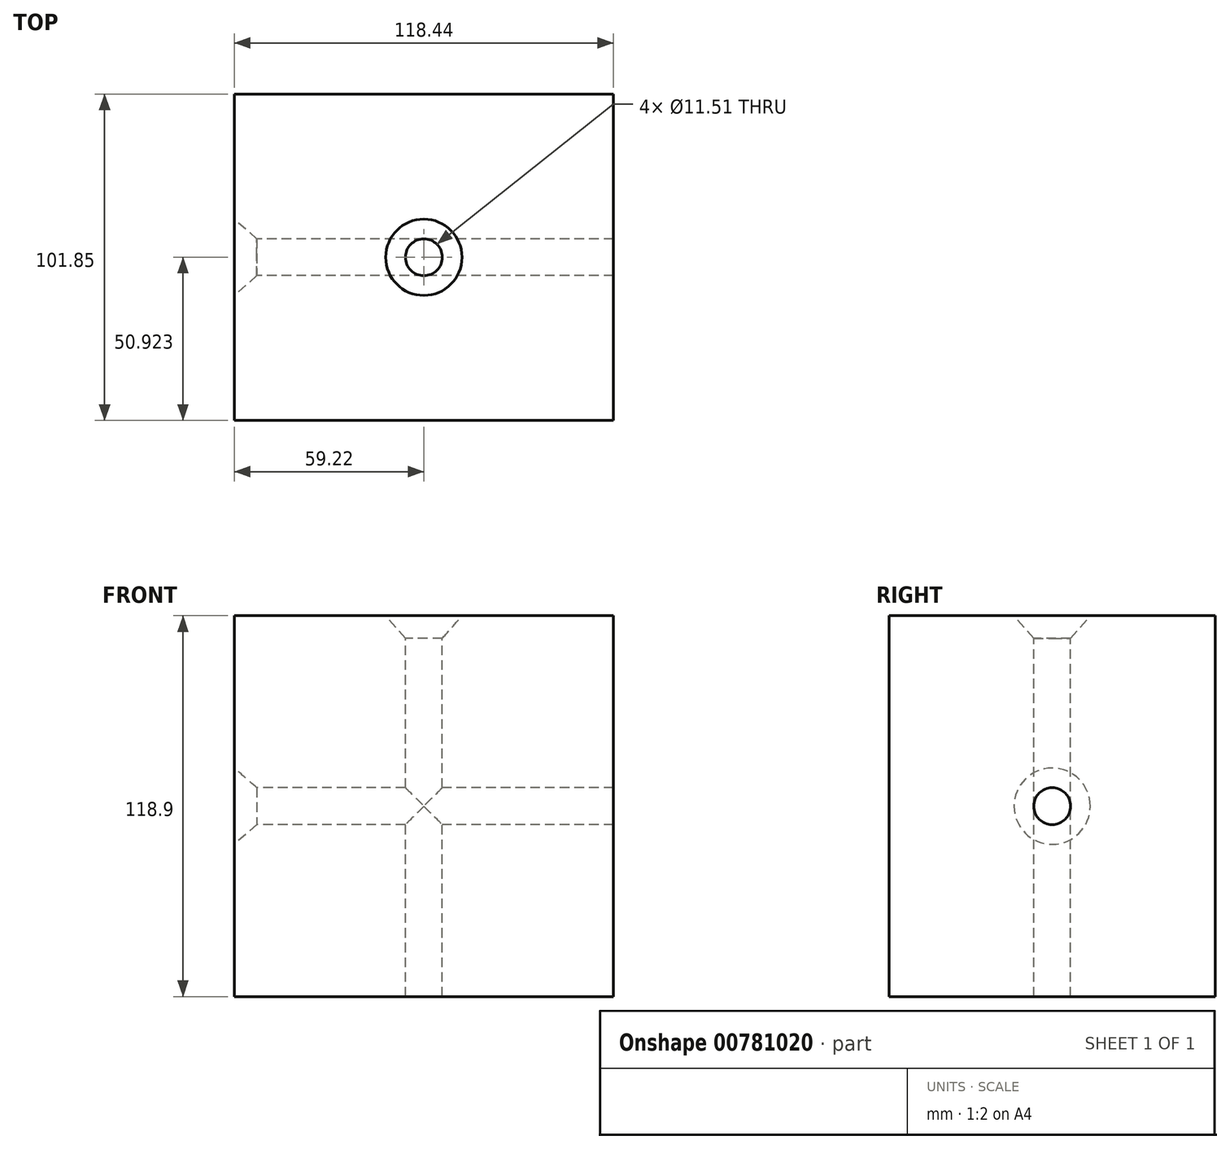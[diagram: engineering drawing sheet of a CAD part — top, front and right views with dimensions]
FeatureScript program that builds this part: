
annotation { "Feature Type Name" : "Feature", "Feature Type Description" : "" }
export const myFeature = defineFeature(function(context is Context, id is Id, definition is map)
    precondition{}
    {
        {
            var Q0;
            Q0=qCreatedBy(makeId("Front.planeOp"),FACE);
            var sketch = newSketch(context, id + "F0", { "sketchPlane" : qUnion([Q0])});
            skLineSegment(sketch, "E0.bottom", {"start": v(59.22, 59.45) * mm, "end": v(-59.22, 59.45) * mm});
            skLineSegment(sketch, "E0.top", {"start": v(59.22, -59.45) * mm, "end": v(-59.22, -59.45) * mm});
            skLineSegment(sketch, "E0.left", {"start": v(59.22, 59.45) * mm, "end": v(59.22, -59.45) * mm});
            skLineSegment(sketch, "E0.right", {"start": v(-59.22, 59.45) * mm, "end": v(-59.22, -59.45) * mm});
            skPoint(sketch, "E0.middle", {"position": v(0, 0) * mm});
            skSolve(sketch);
        }
        {
            var Q0;
            Q0 = qSketchRegion(id + "F0", true);
            extrude(context, id + "F1", {"entities" : qUnion([Q0]), "depth" : 101.85 * mm, "offsetDistance" : 25.4 * mm});
        }
        {
            var Q0;
            Q0=makeQuery(id+"F1.opExtrude","SWEPT_FACE",FACE,{"disambiguationData":[OSD([sQuery(id+"F0.wireOp",EDGE,"E0.bottom")])]});
            var sketch = newSketch(context, id + "F2", { "sketchPlane" : qUnion([Q0])});
            skPoint(sketch, "E1", {"position": v(0, -50.93) * mm});
            skPoint(sketch, "E1.positionSnap0", {"position": v(59.22, -50.93) * mm});
            skPoint(sketch, "E2", {"position": v(25.17, -28.36) * mm});
            skSolve(sketch);
        }
        {
            var Q0;
            Q0=makeQuery(id+"F1.opExtrude","SWEPT_FACE",FACE,{"disambiguationData":[OSD([sQuery(id+"F0.wireOp",EDGE,"E0.right")])]});
            var sketch = newSketch(context, id + "F3", { "sketchPlane" : qUnion([Q0])});
            skPoint(sketch, "E3", {"position": v(50.93, 0) * mm});
            skPoint(sketch, "E3.positionSnap0", {"position": v(50.93, 59.45) * mm});
            skPoint(sketch, "E4", {"position": v(80.46, 30.35) * mm});
            skSolve(sketch);
        }
        {
            var Q0;
            Q0=sQuery(id+"F3.wireOp",VERTEX,"E3");
            var Q1;
            Q1=sQuery(id+"F2.wireOp",VERTEX,"E1");
            var Q2;
            Q2=makeQuery(id+"F1.opExtrude","SWEPT_BODY",BODY,{"disambiguationData":[OSD([sQuery(id+"F0.wireOp",EDGE,"E0.bottom"),sQuery(id+"F0.wireOp",EDGE,"E0.top"),sQuery(id+"F0.wireOp",EDGE,"E0.left"),sQuery(id+"F0.wireOp",EDGE,"E0.right")])]});
            hole(context, id + "F4", {"style" : HoleStyle.C_SINK, "endStyle" : HoleEndStyle.THROUGH, "standardTappedOrClearance" : lookupTablePath({ "standard" : "ANSI", "engagement" : "75%", "pitch" : "20 tpi", "size" : "1/2", "type" : "Tapped" }), "standardBlindInLast" : lookupTablePath({ "standard" : "ANSI", "engagement" : "75%", "pitch" : "20 tpi", "size" : "1/2", "type" : "Tapped" }), "holeDiameter" : 11.5 * mm, "cSinkDiameter" : 23.83 * mm, "cSinkAngle" : 82 * degree, "majorDiameter" : 12.7 * mm, "showTappedDepth" : true, "isTappedThrough" : true, "tappedDepth" : 13.94 * mm, "tapClearance" : 3, "locations" : qUnion([Q0, Q1]), "scope" : qUnion([Q2])});
        }
    });
